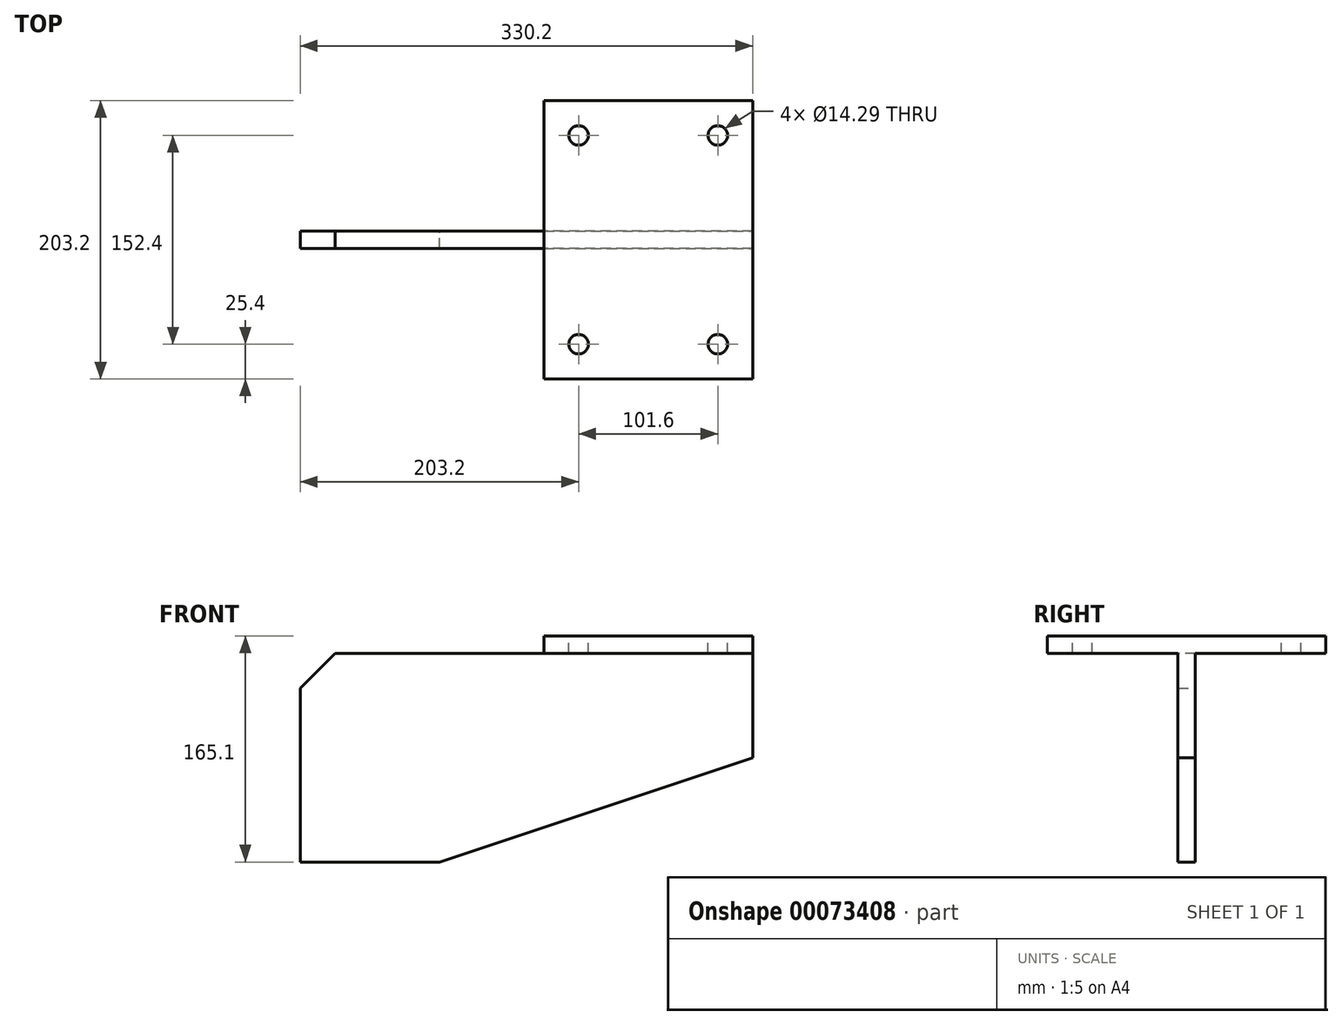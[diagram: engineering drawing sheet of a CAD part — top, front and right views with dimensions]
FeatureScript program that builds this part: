
annotation { "Feature Type Name" : "Feature", "Feature Type Description" : "" }
export const myFeature = defineFeature(function(context is Context, id is Id, definition is map)
    precondition{}
    {
        {
            var Q0;
            Q0=qCreatedBy(makeId("Front.planeOp"),FACE);
            var sketch = newSketch(context, id + "F0", { "sketchPlane" : qUnion([Q0])});
            skLineSegment(sketch, "E0", {"start": v(0, 0) * mm, "end": v(-177.8, 0) * mm, "construction": true});
            skLineSegment(sketch, "E1", {"start": v(0, 0) * mm, "end": v(0, 12.7) * mm, "construction": true});
            skLineSegment(sketch, "E2", {"start": v(0, 12.7) * mm, "end": v(152.4, 12.7) * mm, "construction": true});
            skLineSegment(sketch, "E3.bottom", {"start": v(-177.8, 0) * mm, "end": v(152.4, 0) * mm});
            skLineSegment(sketch, "E3.top", {"start": v(-177.8, -152.4) * mm, "end": v(-76.2, -152.4) * mm});
            skLineSegment(sketch, "E3.left", {"start": v(-177.8, 0) * mm, "end": v(-177.8, -152.4) * mm});
            skLineSegment(sketch, "E3.right", {"start": v(152.4, 0) * mm, "end": v(152.4, -76.2) * mm});
            skLineSegment(sketch, "E4", {"start": v(152.4, -76.2) * mm, "end": v(-76.2, -152.4) * mm});
            skPoint(sketch, "E5.orphan", {"position": v(152.4, -152.4) * mm});
            skSolve(sketch);
        }
        {
            var Q0;
            Q0=makeQuery(id+"F0.imprint","IMPRINT",FACE,{"disambiguationData":[TD([[makeQuery(id+"F0.imprint","IMPRINT",EDGE,{"derivedFrom":sQuery(id+"F0.wireOp",EDGE,"E3.bottom")}),-1.0]])]});
            extrude(context, id + "F1", {"entities" : qUnion([Q0]), "endBound" : BoundingType.SYMMETRIC, "depth" : 12.7 * mm});
        }
        {
            var Q0;
            Q0=makeQuery(id+"F1.opExtrude","SWEPT_FACE",FACE,{"disambiguationData":[OSD([sQuery(id+"F0.wireOp",EDGE,"E3.bottom")])]});
            var sketch = newSketch(context, id + "F2", { "sketchPlane" : qUnion([Q0])});
            skLineSegment(sketch, "E6", {"start": v(152.4, 0) * mm, "end": v(-188.29, 0) * mm, "construction": true});
            skPoint(sketch, "E6.endSnap0", {"position": v(-177.8, 0) * mm});
            skLineSegment(sketch, "E7", {"start": v(152.4, 101.6) * mm, "end": v(152.4, -101.6) * mm, "construction": true});
            skLineSegment(sketch, "E8.bottom", {"start": v(152.4, 101.6) * mm, "end": v(0, 101.6) * mm});
            skLineSegment(sketch, "E8.top", {"start": v(152.4, -101.6) * mm, "end": v(0, -101.6) * mm});
            skLineSegment(sketch, "E8.left", {"start": v(152.4, 101.6) * mm, "end": v(152.4, -101.6) * mm});
            skLineSegment(sketch, "E8.right", {"start": v(0, 101.6) * mm, "end": v(0, -101.6) * mm});
            skSolve(sketch);
        }
        {
            var Q0;
            Q0 = qSketchRegion(id + "F2", true);
            extrude(context, id + "F3", {"entities" : qUnion([Q0]), "operationType" : NewBodyOperationType.ADD, "depth" : 12.7 * mm});
        }
        {
            var Q0;
            Q0=makeQuery(id+"F3.opExtrude","CAP_FACE",FACE,{"disambiguationData":[OSD([sQuery(id+"F2.wireOp",EDGE,"E8.bottom"),sQuery(id+"F2.wireOp",EDGE,"E8.top"),sQuery(id+"F2.wireOp",EDGE,"E8.left"),sQuery(id+"F2.wireOp",EDGE,"E8.right")])],"isStart":false});
            var sketch = newSketch(context, id + "F4", { "sketchPlane" : qUnion([Q0])});
            skLineSegment(sketch, "E9.bottom", {"start": v(127, 76.2) * mm, "end": v(25.4, 76.2) * mm, "construction": true});
            skLineSegment(sketch, "E9.top", {"start": v(127, -76.2) * mm, "end": v(25.4, -76.2) * mm, "construction": true});
            skLineSegment(sketch, "E9.left", {"start": v(127, 76.2) * mm, "end": v(127, -76.2) * mm, "construction": true});
            skLineSegment(sketch, "E9.right", {"start": v(25.4, 76.2) * mm, "end": v(25.4, -76.2) * mm, "construction": true});
            skPoint(sketch, "E10", {"position": v(25.4, 76.2) * mm});
            skPoint(sketch, "E11", {"position": v(127, 76.2) * mm});
            skPoint(sketch, "E12", {"position": v(127, -76.2) * mm});
            skPoint(sketch, "E13", {"position": v(25.4, -76.2) * mm});
            skSolve(sketch);
        }
        {
            var Q0;
            Q0=sQuery(id+"F4.wireOp",VERTEX,"E10");
            var Q1;
            Q1=sQuery(id+"F4.wireOp",VERTEX,"E11");
            var Q2;
            Q2=sQuery(id+"F4.wireOp",VERTEX,"E12");
            var Q3;
            Q3=sQuery(id+"F4.wireOp",VERTEX,"E13");
            var Q4;
            Q4=makeQuery(id+"F1.opExtrude","SWEPT_BODY",BODY,{"disambiguationData":[OSD([sQuery(id+"F0.wireOp",EDGE,"E3.bottom"),sQuery(id+"F0.wireOp",EDGE,"E3.top"),sQuery(id+"F0.wireOp",EDGE,"E3.left"),sQuery(id+"F0.wireOp",EDGE,"E3.right"),sQuery(id+"F0.wireOp",EDGE,"E4")])]});
            hole(context, id + "F5", {"style" : HoleStyle.SIMPLE, "holeDiameter" : 14.29 * mm, "endStyle" : HoleEndStyle.THROUGH, "locations" : qUnion([Q0, Q1, Q2, Q3]), "scope" : qUnion([Q4])});
        }
        {
            var Q0;
            Q0=makeQuery(id+"F1.opExtrude","SWEPT_EDGE",EDGE,{"disambiguationData":[OSD([sQuery(id+"F0.wireOp",EDGE,"E3.bottom"),sQuery(id+"F0.wireOp",EDGE,"E3.left")])]});
            chamfer(context, id + "F6", {"entities" : qUnion([Q0]), "width" : 25.4 * mm, "tangentPropagation" : true});
        }
    });
